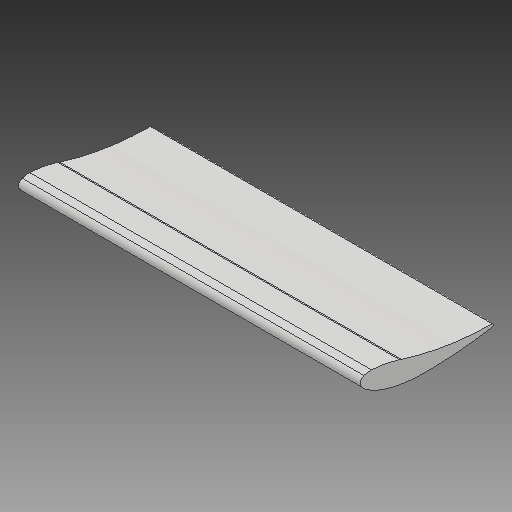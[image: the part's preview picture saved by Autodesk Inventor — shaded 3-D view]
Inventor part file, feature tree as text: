
AUTODESK INVENTOR PART (.ipt)
format: ipt  version: 2018.2 (Build 222227000, 227)  size: 168,960 bytes
history: native  units: mm
features: other x4, extrude x2, sketch x2, fillet x1, projected_geometry x1
ambient origin geometry x8: Origin, YZ Plane, XZ Plane, XY Plane, X Axis, Y Axis, Z Axis, Center Point
bodies: Body1 (feature_tree)
feature tree (10):
  other  "naca97.ipt"
  extrude  "押し出し1"  Depth=110.0mm
  fillet  "フィレット1"  Radius=220.0mm
  extrude  "押し出し2"  Depth=1200.0mm
  other  "ソリッド1::naca97.ipt"
  other  "TaggingFeature1"
  sketch  "スケッチ1"
  sketch  "スケッチ2"
  projected_geometry  "投影ループ1"
  other  "ソリッド1"
